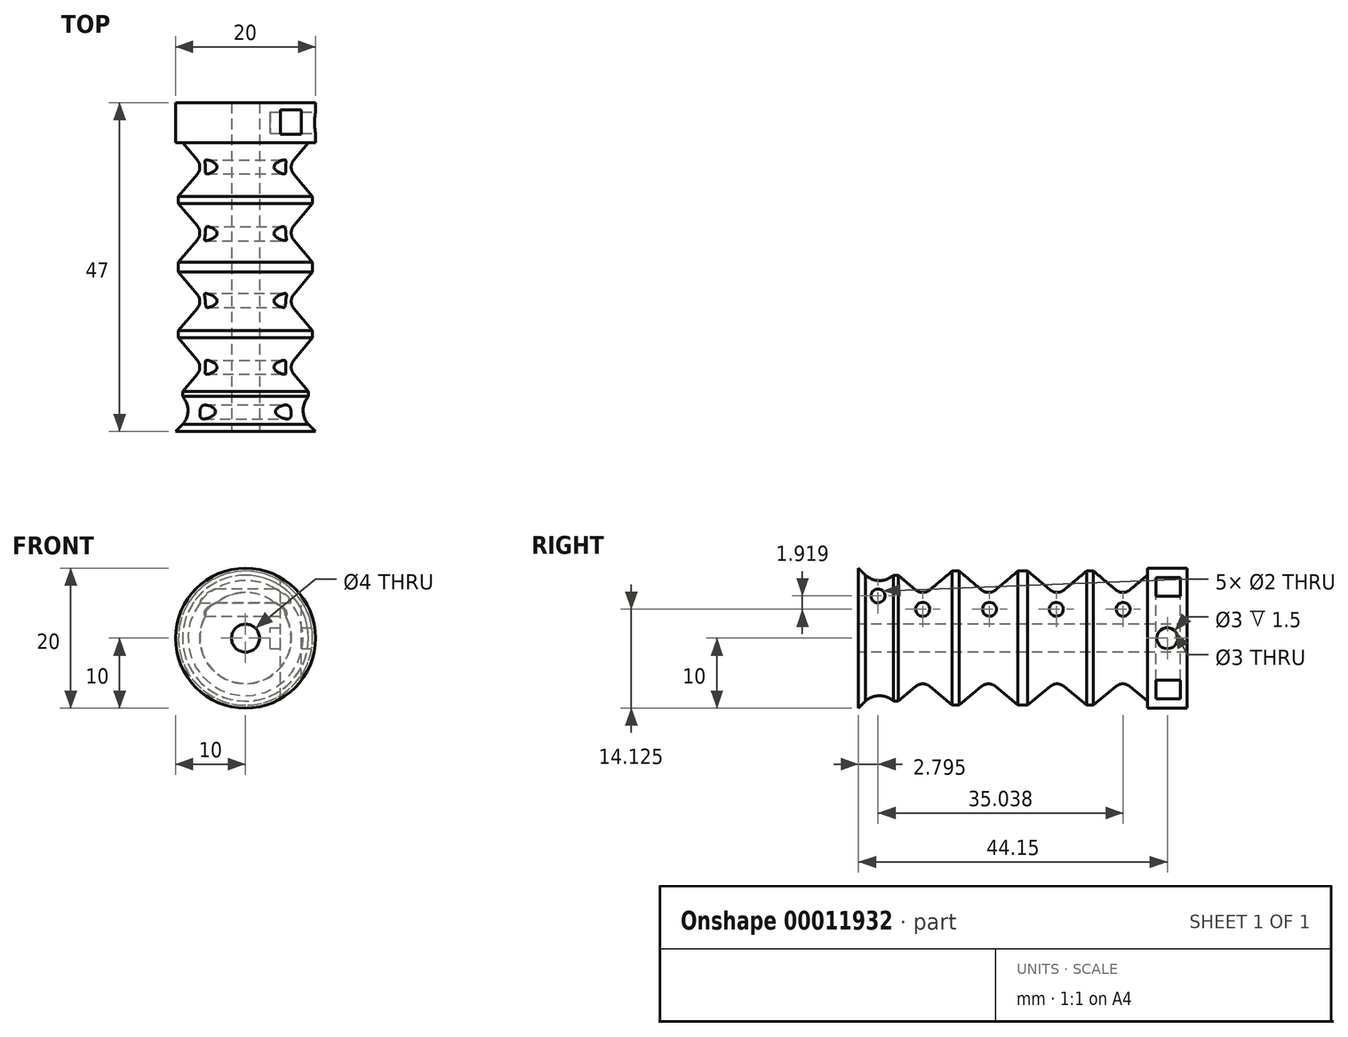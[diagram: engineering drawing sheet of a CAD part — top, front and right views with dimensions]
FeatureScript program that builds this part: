
annotation { "Feature Type Name" : "Feature", "Feature Type Description" : "" }
export const myFeature = defineFeature(function(context is Context, id is Id, definition is map)
    precondition{}
    {
        {
            var Q0;
            Q0=qCreatedBy(makeId("Front.planeOp"),FACE);
            var sketch = newSketch(context, id + "F0", { "sketchPlane" : qUnion([Q0])});
            skCircle(sketch, "E0", {"center": v(0, 0) * mm, "radius": 10 * mm});
            skSolve(sketch);
        }
        {
            var Q0;
            Q0=makeQuery(id+"F0.imprint","IMPRINT",FACE,{"disambiguationData":[TD([[makeQuery(id+"F0.imprint","IMPRINT",EDGE,{"derivedFrom":sQuery(id+"F0.wireOp",EDGE,"E0")}),1.0]])]});
            extrude(context, id + "F1", {"entities" : qUnion([Q0]), "depth" : 47 * mm});
        }
        {
            var Q0;
            Q0=makeQuery(id+"F1.opExtrude","CAP_FACE",FACE,{"disambiguationData":[OSD([sQuery(id+"F0.wireOp",EDGE,"E0")])],"isStart":false});
            var sketch = newSketch(context, id + "F2", { "sketchPlane" : qUnion([Q0])});
            skCircle(sketch, "E1", {"center": v(0, 0) * mm, "radius": 2 * mm});
            skSolve(sketch);
        }
        {
            var Q0;
            Q0=qSketchRegion(id+"F2",true);
            extrude(context, id + "F3", {"entities" : qUnion([Q0]), "operationType" : NewBodyOperationType.REMOVE, "endBound" : BoundingType.THROUGH_ALL, "oppositeDirection" : true, "depth" : 25 * mm});
        }
        {
            var Q0;
            Q0=qCreatedBy(makeId("Right.planeOp"),FACE);
            var sketch = newSketch(context, id + "F4", { "sketchPlane" : qUnion([Q0])});
            skArc(sketch, "E2", {"start": v(-46, 9) * mm, "mid": v(-44, 8.24) * mm, "end": v(-42, 9) * mm});
            skLineSegment(sketch, "E3.0", {"start": v(-47, -10) * mm, "end": v(-47, 10) * mm, "construction": true});
            skLineSegment(sketch, "E4", {"start": v(-47, 0) * mm, "end": v(0, 0) * mm, "construction": true});
            skLineSegment(sketch, "E5", {"start": v(-23.5, 0) * mm, "end": v(-23.5, 16.63) * mm, "construction": true});
            skLineSegment(sketch, "E6", {"start": v(-42, 9) * mm, "end": v(-41.3, 9) * mm});
            skLineSegment(sketch, "E7", {"start": v(-41.3, 9) * mm, "end": v(-38.8, 6.9) * mm});
            skArc(sketch, "E8", {"start": v(-38.8, 6.9) * mm, "mid": v(-37.8, 6.54) * mm, "end": v(-36.8, 6.9) * mm});
            skLineSegment(sketch, "E9", {"start": v(-37.8, 6.54) * mm, "end": v(-37.8, 14.57) * mm, "construction": true});
            skLineSegment(sketch, "E10.0.MirrorCS", {"start": v(-33.6, 9.59) * mm, "end": v(-36.8, 6.9) * mm});
            skLineSegment(sketch, "E11", {"start": v(-46, 9) * mm, "end": v(-47, 10) * mm});
            skLineSegment(sketch, "E12", {"start": v(-47, 10) * mm, "end": v(-47, 11.4) * mm});
            skLineSegment(sketch, "E13", {"start": v(-47, 11.4) * mm, "end": v(-23.5, 11.4) * mm});
            skPoint(sketch, "E14.orphan", {"position": v(-34.3, 9) * mm});
            skLineSegment(sketch, "E15", {"start": v(-33.6, 9.59) * mm, "end": v(-33.1, 9.59) * mm});
            skLineSegment(sketch, "E16", {"start": v(-33.1, 9.59) * mm, "end": v(-33.1, 15.25) * mm, "construction": true});
            skArc(sketch, "E17.0.MirrorCS", {"start": v(-27.4, 6.9) * mm, "mid": v(-28.4, 6.54) * mm, "end": v(-29.4, 6.9) * mm});
            skLineSegment(sketch, "E17.1.MirrorCS", {"start": v(-32.6, 9.59) * mm, "end": v(-33.1, 9.59) * mm});
            skLineSegment(sketch, "E17.2.MirrorCS", {"start": v(-32.6, 9.59) * mm, "end": v(-29.4, 6.9) * mm});
            skLineSegment(sketch, "E18", {"start": v(-27.4, 6.9) * mm, "end": v(-24.2, 9.59) * mm});
            skLineSegment(sketch, "E19", {"start": v(-24.2, 9.59) * mm, "end": v(-23.5, 9.59) * mm});
            skLineSegment(sketch, "E20.0.MirrorCS", {"start": v(-22.8, 9.59) * mm, "end": v(-23.5, 9.59) * mm});
            skLineSegment(sketch, "E20.2.MirrorCS", {"start": v(-14.4, 9.59) * mm, "end": v(-13.9, 9.59) * mm});
            skLineSegment(sketch, "E20.3.MirrorCS", {"start": v(-13.4, 9.59) * mm, "end": v(-13.9, 9.59) * mm});
            skLineSegment(sketch, "E20.5.MirrorCS", {"start": v(-13.9, 9.59) * mm, "end": v(-13.9, 15.25) * mm, "construction": true});
            skLineSegment(sketch, "E20.6.MirrorCS", {"start": v(-14.4, 9.59) * mm, "end": v(-17.6, 6.9) * mm});
            skLineSegment(sketch, "E20.7.MirrorCS", {"start": v(-19.6, 6.9) * mm, "end": v(-22.8, 9.59) * mm});
            skPoint(sketch, "E20.8.MirrorP", {"position": v(-12.7, 9) * mm});
            skLineSegment(sketch, "E20.9.MirrorCS", {"start": v(0, -10) * mm, "end": v(0, 10) * mm, "construction": true});
            skLineSegment(sketch, "E20.10.MirrorCS", {"start": v(-9.2, 6.54) * mm, "end": v(-9.2, 14.57) * mm, "construction": true});
            skLineSegment(sketch, "E20.12.MirrorCS", {"start": v(-5.7, 9) * mm, "end": v(-8.2, 6.9) * mm});
            skLineSegment(sketch, "E20.13.MirrorCS", {"start": v(0, 11.4) * mm, "end": v(-23.5, 11.4) * mm});
            skLineSegment(sketch, "E20.14.MirrorCS", {"start": v(-13.4, 9.59) * mm, "end": v(-10.2, 6.9) * mm});
            skArc(sketch, "E20.15.MirrorCS", {"start": v(-8.2, 6.9) * mm, "mid": v(-9.2, 6.54) * mm, "end": v(-10.2, 6.9) * mm});
            skLineSegment(sketch, "E20.16.MirrorCS", {"start": v(0, 10) * mm, "end": v(0, 11.4) * mm});
            skArc(sketch, "E20.17.MirrorCS", {"start": v(-19.6, 6.9) * mm, "mid": v(-18.6, 6.54) * mm, "end": v(-17.6, 6.9) * mm});
            skLineSegment(sketch, "E21", {"start": v(-5.7, 9) * mm, "end": v(-5.7, 10) * mm});
            skLineSegment(sketch, "E22", {"start": v(-5.7, 10) * mm, "end": v(0, 10) * mm});
            skSolve(sketch);
        }
        {
            var Q0;
            Q0=makeQuery(id+"F4.imprint","IMPRINT",FACE,{"disambiguationData":[TD([[makeQuery(id+"F4.imprint","IMPRINT",EDGE,{"derivedFrom":sQuery(id+"F4.wireOp",EDGE,"E2")}),1.0]])]});
            var Q1;
            Q1=sQuery(id+"F4.wireOp",EDGE,"E4");
            revolve(context, id + "F5", {"operationType" : NewBodyOperationType.REMOVE, "entities" : qUnion([Q0]), "axis" : qUnion([Q1]), "revolveType" : RevolveType.FULL, "oppositeDirection" : true});
        }
        {
            var Q0;
            Q0=qCreatedBy(makeId("Right.planeOp"),FACE);
            cPlane(context, id + "F6", {"entities" : qUnion([Q0]), "cplaneType" : CPlaneType.OFFSET, "offset" : 10 * mm, "width" : 150 * mm, "height" : 150 * mm});
        }
        {
            var Q0;
            Q0=qCreatedBy(makeId("Top.planeOp"),FACE);
            var sketch = newSketch(context, id + "F7", { "sketchPlane" : qUnion([Q0])});
            skLineSegment(sketch, "E23.bottom", {"start": v(8, -4.5) * mm, "end": v(5, -4.5) * mm});
            skLineSegment(sketch, "E23.top", {"start": v(8, -1) * mm, "end": v(5, -1) * mm});
            skLineSegment(sketch, "E23.left", {"start": v(8, -4.5) * mm, "end": v(8, -1) * mm});
            skLineSegment(sketch, "E23.right", {"start": v(5, -4.5) * mm, "end": v(5, -1) * mm});
            skLineSegment(sketch, "E24", {"start": v(6.5, -4.5) * mm, "end": v(6.5, -1) * mm, "construction": true});
            skPoint(sketch, "E25", {"position": v(6.5, -2.75) * mm});
            skSolve(sketch);
        }
        {
            var Q0;
            Q0=qSketchRegion(id+"F7",true);
            extrude(context, id + "F8", {"entities" : qUnion([Q0]), "operationType" : NewBodyOperationType.REMOVE, "oppositeDirection" : true, "depth" : 25 * mm, "hasSecondDirection" : true, "secondDirectionOppositeDirection" : false, "secondDirectionDepth" : 25 * mm});
        }
        {
            var Q0;
            Q0=qCreatedBy(id+"F6.planeOp",FACE);
            var sketch = newSketch(context, id + "F9", { "sketchPlane" : qUnion([Q0])});
            skCircle(sketch, "E26", {"center": v(-2.85, 0) * mm, "radius": 1.5 * mm});
            skLineSegment(sketch, "E27", {"start": v(0, 0) * mm, "end": v(-5.7, 0) * mm, "construction": true});
            skSolve(sketch);
        }
        {
            var Q0;
            Q0=qSketchRegion(id+"F9",true);
            extrude(context, id + "F10", {"entities" : qUnion([Q0]), "operationType" : NewBodyOperationType.REMOVE, "oppositeDirection" : true, "depth" : 6.5 * mm});
        }
        {
            var Q0;
            Q0=qCreatedBy(makeId("Right.planeOp"),FACE);
            var sketch = newSketch(context, id + "F11", { "sketchPlane" : qUnion([Q0])});
            skCircle(sketch, "E28", {"center": v(-44.2, 6.04) * mm, "radius": 1 * mm});
            skCircle(sketch, "E29", {"center": v(-37.82, 4.12) * mm, "radius": 1 * mm});
            skCircle(sketch, "E30.1.0.0", {"center": v(-28.27, 4.12) * mm, "radius": 1 * mm});
            skCircle(sketch, "E30.2.0.0", {"center": v(-18.72, 4.12) * mm, "radius": 1 * mm});
            skCircle(sketch, "E30.3.0.0", {"center": v(-9.17, 4.12) * mm, "radius": 1 * mm});
            skLineSegment(sketch, "E30.direction1", {"start": v(-37.82, 4.12) * mm, "end": v(-28.27, 4.12) * mm, "construction": true});
            skSolve(sketch);
        }
        {
            var Q0;
            Q0 = qSketchRegion(id + "F11", true);
            extrude(context, id + "F12", {"entities" : qUnion([Q0]), "operationType" : NewBodyOperationType.REMOVE, "endBound" : BoundingType.THROUGH_ALL, "oppositeDirection" : true, "depth" : 25 * mm, "hasSecondDirection" : true, "secondDirectionBound" : SecondDirectionBoundingType.THROUGH_ALL, "secondDirectionOppositeDirection" : false, "secondDirectionDepth" : 25 * mm});
        }
    });
